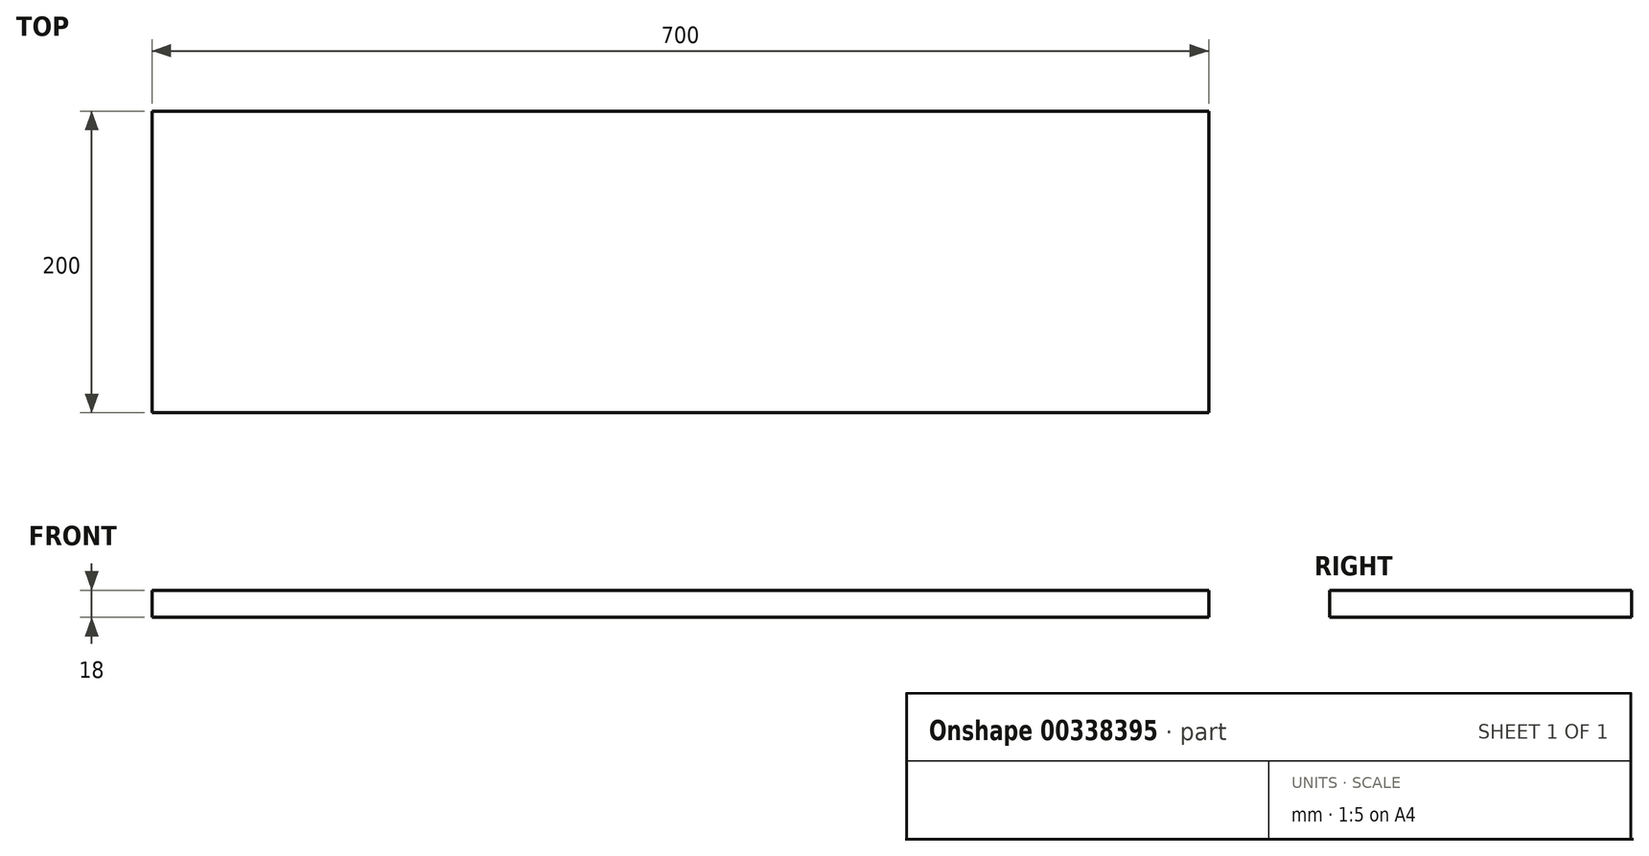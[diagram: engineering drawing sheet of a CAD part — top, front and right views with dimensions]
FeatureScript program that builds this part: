
annotation { "Feature Type Name" : "Feature", "Feature Type Description" : "" }
export const myFeature = defineFeature(function(context is Context, id is Id, definition is map)
    precondition{}
    {
        {
            var Q0;
            Q0=qCreatedBy(makeId("Top.planeOp"),FACE);
            var sketch = newSketch(context, id + "F0", { "sketchPlane" : qUnion([Q0])});
            skLineSegment(sketch, "E0.bottom", {"start": v(-350, -100) * mm, "end": v(350, -100) * mm});
            skLineSegment(sketch, "E0.top", {"start": v(-350, 100) * mm, "end": v(350, 100) * mm});
            skLineSegment(sketch, "E0.left", {"start": v(-350, -100) * mm, "end": v(-350, 100) * mm});
            skLineSegment(sketch, "E0.right", {"start": v(350, -100) * mm, "end": v(350, 100) * mm});
            skPoint(sketch, "E0.middle", {"position": v(0, 0) * mm});
            skSolve(sketch);
        }
        {
            var Q0;
            Q0=makeQuery(id+"F0.imprint","IMPRINT",FACE,{"disambiguationData":[TD([[makeQuery(id+"F0.imprint","IMPRINT",EDGE,{"derivedFrom":sQuery(id+"F0.wireOp",EDGE,"E0.bottom")}),1.0]])]});
            extrude(context, id + "F1", {"entities" : qUnion([Q0]), "depth" : 18 * mm});
        }
    });
